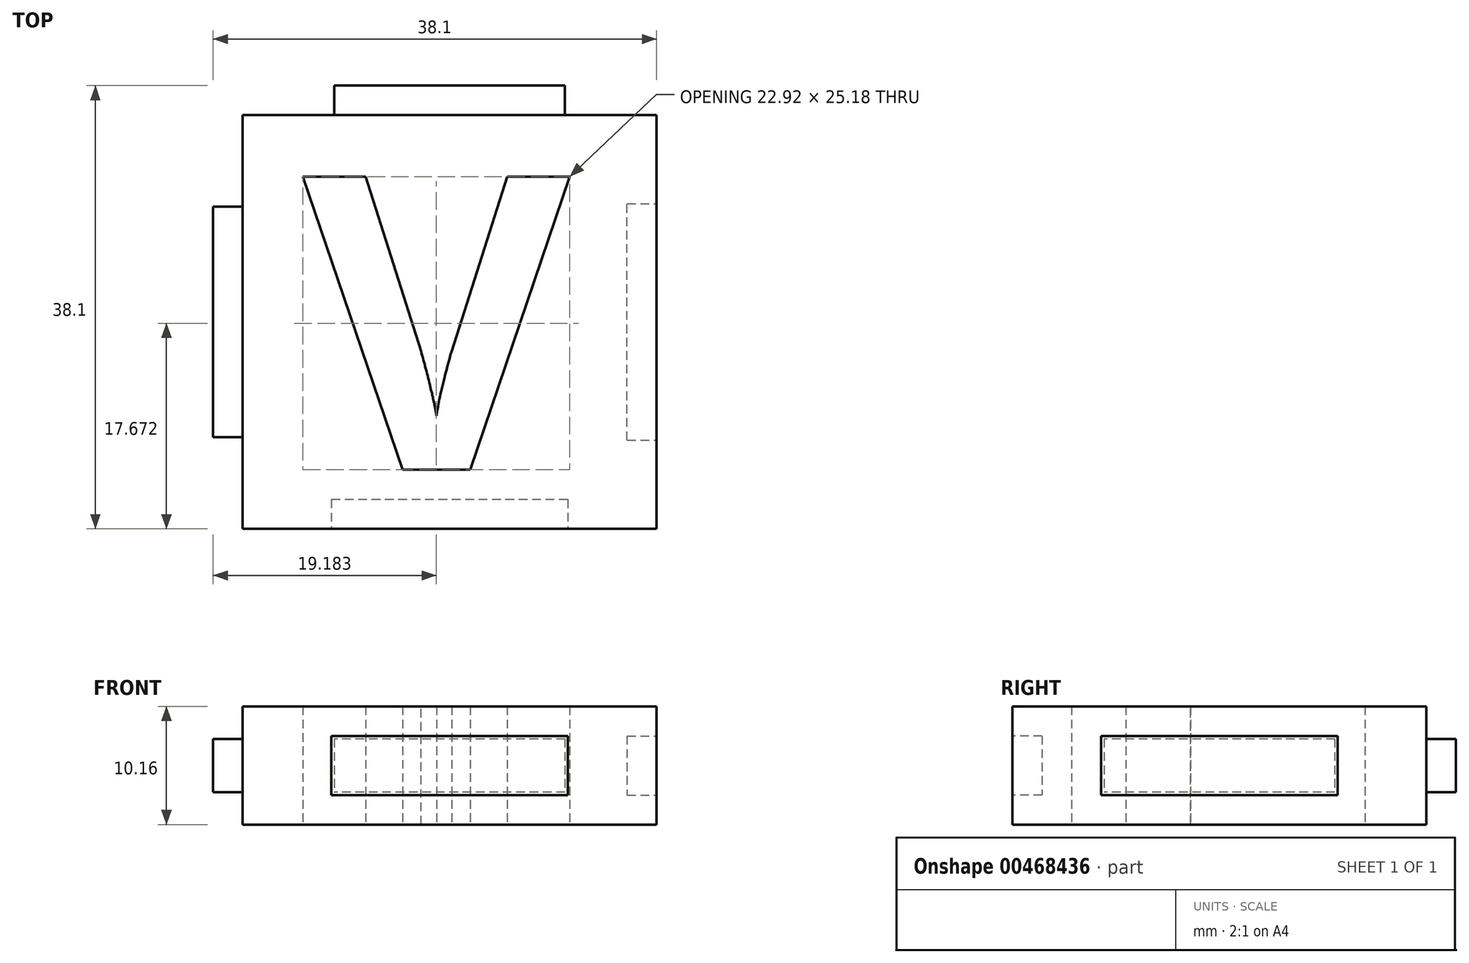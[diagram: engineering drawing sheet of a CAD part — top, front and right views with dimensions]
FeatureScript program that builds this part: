
annotation { "Feature Type Name" : "Feature", "Feature Type Description" : "" }
export const myFeature = defineFeature(function(context is Context, id is Id, definition is map)
    precondition{}
    {
        {
            var Q0;
            Q0=qCreatedBy(makeId("Top.planeOp"),FACE);
            var sketch = newSketch(context, id + "F0", { "sketchPlane" : qUnion([Q0])});
            skLineSegment(sketch, "E0.bottom", {"start": v(-17.78, 17.78) * mm, "end": v(17.78, 17.78) * mm});
            skLineSegment(sketch, "E0.top", {"start": v(-17.78, -17.78) * mm, "end": v(17.78, -17.78) * mm});
            skLineSegment(sketch, "E0.left", {"start": v(-17.78, 17.78) * mm, "end": v(-17.78, -17.78) * mm});
            skLineSegment(sketch, "E0.right", {"start": v(17.78, 17.78) * mm, "end": v(17.78, -17.78) * mm});
            skText(sketch, "E1", { "text": "V", "fontName": "OpenSans-Bold.ttf"});
            const initialGuessF0  = {"E1": [-0.0126, -0.0127, 1, 0, 0.0254]};
            skSetInitialGuess(sketch, initialGuessF0);
            skSolve(sketch);
        }
        {
            var Q0;
            Q0=qSketchRegion(id+"F0",true);
            extrude(context, id + "F1", {"entities" : qUnion([Q0]), "endBound" : BoundingType.SYMMETRIC, "depth" : 10.16 * mm});
        }
        {
            var Q0;
            Q0=makeQuery(id+"F1.opExtrude","SWEPT_FACE",FACE,{"disambiguationData":[OSD([sQuery(id+"F0.wireOp",EDGE,"E0.bottom")])]});
            var sketch = newSketch(context, id + "F2", { "sketchPlane" : qUnion([Q0])});
            skLineSegment(sketch, "E2.bottom", {"start": v(-9.9, 2.29) * mm, "end": v(9.9, 2.29) * mm});
            skLineSegment(sketch, "E2.top", {"start": v(-9.9, -2.29) * mm, "end": v(9.9, -2.29) * mm});
            skLineSegment(sketch, "E2.left", {"start": v(-9.9, 2.29) * mm, "end": v(-9.9, -2.29) * mm});
            skLineSegment(sketch, "E2.right", {"start": v(9.9, 2.29) * mm, "end": v(9.9, -2.29) * mm});
            skSolve(sketch);
        }
        {
            var Q0;
            Q0=qSketchRegion(id+"F2",true);
            extrude(context, id + "F3", {"entities" : qUnion([Q0]), "operationType" : NewBodyOperationType.ADD, "depth" : 2.54 * mm});
        }
        {
            var Q0;
            Q0=makeQuery(id+"F1.opExtrude","SWEPT_FACE",FACE,{"disambiguationData":[OSD([sQuery(id+"F0.wireOp",EDGE,"E0.left")])]});
            var sketch = newSketch(context, id + "F4", { "sketchPlane" : qUnion([Q0])});
            skLineSegment(sketch, "E3.bottom", {"start": v(-9.9, 2.29) * mm, "end": v(9.9, 2.29) * mm});
            skLineSegment(sketch, "E3.top", {"start": v(-9.9, -2.29) * mm, "end": v(9.9, -2.29) * mm});
            skLineSegment(sketch, "E3.left", {"start": v(-9.9, 2.29) * mm, "end": v(-9.9, -2.29) * mm});
            skLineSegment(sketch, "E3.right", {"start": v(9.9, 2.29) * mm, "end": v(9.9, -2.29) * mm});
            skSolve(sketch);
        }
        {
            var Q0;
            Q0=qSketchRegion(id+"F4",true);
            extrude(context, id + "F5", {"entities" : qUnion([Q0]), "operationType" : NewBodyOperationType.ADD, "depth" : 2.54 * mm});
        }
        {
            var Q0;
            Q0=makeQuery(id+"F1.opExtrude","SWEPT_FACE",FACE,{"disambiguationData":[OSD([sQuery(id+"F0.wireOp",EDGE,"E0.top")])]});
            var sketch = newSketch(context, id + "F6", { "sketchPlane" : qUnion([Q0])});
            skLineSegment(sketch, "E4.bottom", {"start": v(-10.16, 2.54) * mm, "end": v(10.16, 2.54) * mm});
            skLineSegment(sketch, "E4.top", {"start": v(-10.16, -2.54) * mm, "end": v(10.16, -2.54) * mm});
            skLineSegment(sketch, "E4.left", {"start": v(-10.16, 2.54) * mm, "end": v(-10.16, -2.54) * mm});
            skLineSegment(sketch, "E4.right", {"start": v(10.16, 2.54) * mm, "end": v(10.16, -2.54) * mm});
            skSolve(sketch);
        }
        {
            var Q0;
            Q0=qSketchRegion(id+"F6",true);
            extrude(context, id + "F7", {"entities" : qUnion([Q0]), "operationType" : NewBodyOperationType.REMOVE, "oppositeDirection" : true, "depth" : 2.54 * mm});
        }
        {
            var Q0;
            Q0=makeQuery(id+"F1.opExtrude","SWEPT_FACE",FACE,{"disambiguationData":[OSD([sQuery(id+"F0.wireOp",EDGE,"E0.right")])]});
            var sketch = newSketch(context, id + "F8", { "sketchPlane" : qUnion([Q0])});
            skLineSegment(sketch, "E5.bottom", {"start": v(-10.16, 2.54) * mm, "end": v(10.16, 2.54) * mm});
            skLineSegment(sketch, "E5.top", {"start": v(-10.16, -2.54) * mm, "end": v(10.16, -2.54) * mm});
            skLineSegment(sketch, "E5.left", {"start": v(-10.16, 2.54) * mm, "end": v(-10.16, -2.54) * mm});
            skLineSegment(sketch, "E5.right", {"start": v(10.16, 2.54) * mm, "end": v(10.16, -2.54) * mm});
            skSolve(sketch);
        }
        {
            var Q0;
            Q0=qSketchRegion(id+"F8",true);
            extrude(context, id + "F9", {"entities" : qUnion([Q0]), "operationType" : NewBodyOperationType.REMOVE, "oppositeDirection" : true, "depth" : 2.54 * mm});
        }
    });
